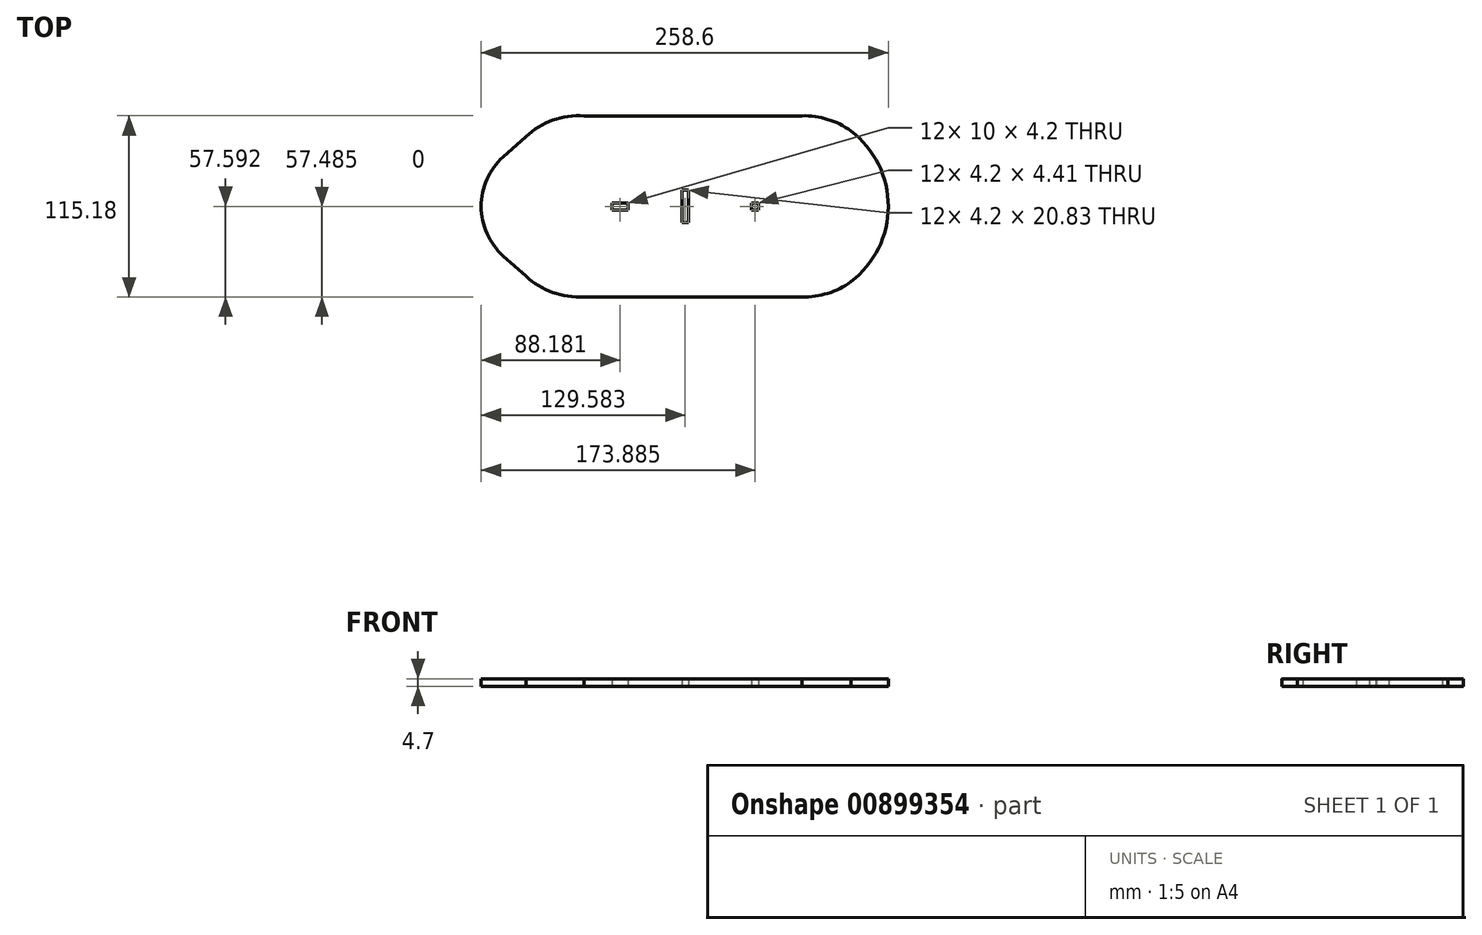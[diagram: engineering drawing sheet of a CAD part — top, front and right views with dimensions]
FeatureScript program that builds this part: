
annotation { "Feature Type Name" : "Feature", "Feature Type Description" : "" }
export const myFeature = defineFeature(function(context is Context, id is Id, definition is map)
    precondition{}
    {
        {
            var Q0;
            Q0=qCreatedBy(makeId("Top.planeOp"),FACE);
            var sketch = newSketch(context, id + "F0", { "sketchPlane" : qUnion([Q0])});
            skPoint(sketch, "E0.middle", {"position": v(-9.6, -416.33) * mm});
            skPoint(sketch, "E1.endSnap0", {"position": v(-84.6, -416.33) * mm});
            skPoint(sketch, "E2", {"position": v(-13.3, -416.33) * mm});
            skPoint(sketch, "E3.orphan", {"position": v(-104.02, -416.33) * mm});
            skPoint(sketch, "E4", {"position": v(-54.7, -416.44) * mm});
            skPoint(sketch, "E5", {"position": v(31.21, -416.33) * mm});
            skLineSegment(sketch, "E6.bottom", {"start": v(-59.7, -414.34) * mm, "end": v(-49.7, -414.34) * mm});
            skLineSegment(sketch, "E6.top", {"start": v(-59.7, -418.54) * mm, "end": v(-49.7, -418.54) * mm});
            skLineSegment(sketch, "E6.left", {"start": v(-59.7, -414.34) * mm, "end": v(-59.7, -418.54) * mm});
            skLineSegment(sketch, "E6.right", {"start": v(-49.7, -414.34) * mm, "end": v(-49.7, -418.54) * mm});
            skLineSegment(sketch, "E7.MirrorCS", {"start": v(28.9, -414.12) * mm, "end": v(28.9, -418.54) * mm});
            skLineSegment(sketch, "E8.MirrorCS", {"start": v(33.1, -414.12) * mm, "end": v(28.9, -414.12) * mm});
            skLineSegment(sketch, "E9.MirrorCS", {"start": v(33.1, -414.12) * mm, "end": v(33.1, -418.54) * mm});
            skLineSegment(sketch, "E10.MirrorCS", {"start": v(33.1, -418.54) * mm, "end": v(28.9, -418.54) * mm});
            skLineSegment(sketch, "E11.bottom", {"start": v(-15.4, -405.91) * mm, "end": v(-11.2, -405.91) * mm});
            skLineSegment(sketch, "E11.top", {"start": v(-15.4, -426.75) * mm, "end": v(-11.2, -426.75) * mm});
            skLineSegment(sketch, "E11.left", {"start": v(-15.4, -405.91) * mm, "end": v(-15.4, -426.75) * mm});
            skLineSegment(sketch, "E11.right", {"start": v(-11.2, -405.91) * mm, "end": v(-11.2, -426.75) * mm});
            skPoint(sketch, "E12.orphan", {"position": v(-84.6, -398.83) * mm});
            skPoint(sketch, "E13.orphan", {"position": v(-84.6, -433.83) * mm});
            skArc(sketch, "E14.4", {"start": v(71.11, -396.63) * mm, "mid": v(71.08, -396.6) * mm, "end": v(71.05, -396.58) * mm});
            skLineSegment(sketch, "E15.0", {"start": v(-77.7, -358.83) * mm, "end": v(60.87, -358.83) * mm});
            skArc(sketch, "E15.1", {"start": v(91.95, -368.5) * mm, "mid": v(77.22, -361.07) * mm, "end": v(60.87, -358.83) * mm});
            skArc(sketch, "E15.2", {"start": v(-77.7, -358.83) * mm, "mid": v(-97.46, -361.64) * mm, "end": v(-114.53, -371.96) * mm});
            skArc(sketch, "E15.3", {"start": v(91.95, -464.16) * mm, "mid": v(115.72, -416.33) * mm, "end": v(91.95, -368.5) * mm});
            skArc(sketch, "E15.4", {"start": v(91.95, -464.16) * mm, "mid": v(77.22, -471.59) * mm, "end": v(60.87, -473.83) * mm});
            skLineSegment(sketch, "E15.5", {"start": v(-77.7, -473.83) * mm, "end": v(60.87, -473.83) * mm});
            skLineSegment(sketch, "E15.6", {"start": v(-114.53, -371.96) * mm, "end": v(-128.88, -384.89) * mm});
            skArc(sketch, "E15.7", {"start": v(-128.88, -384.89) * mm, "mid": v(-142.88, -416.33) * mm, "end": v(-128.88, -447.77) * mm});
            skLineSegment(sketch, "E15.8", {"start": v(-128.88, -447.77) * mm, "end": v(-114.53, -460.7) * mm});
            skArc(sketch, "E15.9", {"start": v(-77.7, -473.83) * mm, "mid": v(-97.46, -471.02) * mm, "end": v(-114.53, -460.7) * mm});
            skLineSegment(sketch, "E16.trimOffspring", {"start": v(65.4, -433.37) * mm, "end": v(65.4, -433.83) * mm});
            skPoint(sketch, "E17.MirrorCS.end.orphan", {"position": v(61.68, -433.83) * mm});
            skPoint(sketch, "E18.orphan", {"position": v(68.07, -432.06) * mm});
            skPoint(sketch, "E19.orphan", {"position": v(68.07, -400.6) * mm});
            skPoint(sketch, "E20.end.orphan", {"position": v(61.68, -398.83) * mm});
            skSolve(sketch);
        }
        {
            var Q0;
            Q0 = qSketchRegion(id + "F0", true);
            extrude(context, id + "F1", {"entities" : qUnion([Q0]), "depth" : 4.7 * mm, "offsetDistance" : 25 * mm});
        }
    });
